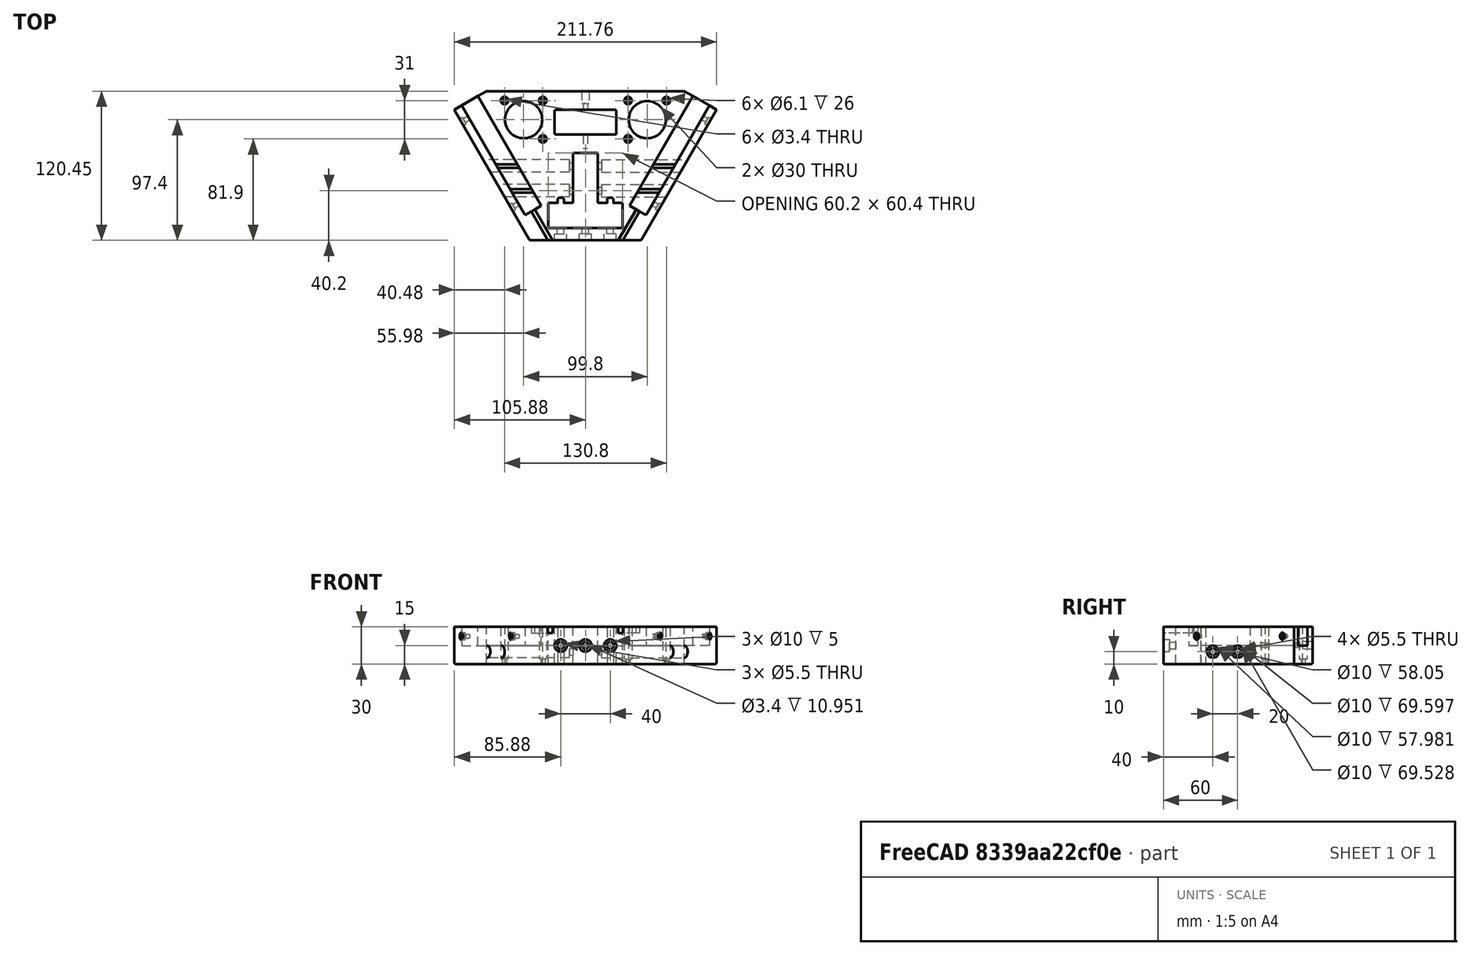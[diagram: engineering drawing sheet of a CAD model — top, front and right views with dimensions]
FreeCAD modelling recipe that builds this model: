
FCSTD DOCUMENT  (FreeCAD 2022.407R26244 +4693 (Git))
Label: as3top_corner
License: All rights reserved
LicenseURL: http://en.wikipedia.org/wiki/All_rights_reserved
objects: Part::FeaturePython×12, App::FeaturePython×2, Part::Feature×1
note: 12 computed .brp shape members not serialized (recipe doc carries the construction recipe); baked Part::Feature solids carry a one-line shape summary decoded from their .brp

FEATURE [App::FeaturePython] Constraints  # WARN: FeaturePython — macro-defined, semantics opaque (R4)
  TreeRank = 0
  _LinkVersion = 1
  _Version = 1
FEATURE [Part::Feature] ShapeCopy  label="TopCorner"
  Placement = pos=(-1.75e-14,-0.999998,-2.49e-14) rot=(0,0,1;0rad)
  TreeRank = 6
  shape: bbox 211.8 x 120.4 x 30 mm, 156 faces (baked)
FEATURE [Part::FeaturePython] Parts  # WARN: FeaturePython — macro-defined, semantics opaque (R4)
  Group = -> [ShapeCopy]
  GroupMode = 0
  TreeRank = 0
  _LinkVersion = 1
FEATURE [Part::FeaturePython] Assembly  label="As3TopCorner"  # WARN: FeaturePython — macro-defined, semantics opaque (R4)
  AutoRelax = true
  BuildShape = 0
  Freeze = false
  Group = -> [Constraints,Elements,Parts]
  TreeRank = 0
  Verbose = false
  _LinkVersion = 1
  _SolverType = 1
  _Version = 1
FEATURE [App::FeaturePython] Elements  # WARN: FeaturePython — macro-defined, semantics opaque (R4)
  Group = -> [Element,Element001,Element002,Element004,Element005,Element006,Element007,Element008,Element009,Element010]
  TreeRank = 0
  _LinkVersion = 1
FEATURE [Part::FeaturePython] Element  label="FaceHsup"  # link proxy (typed FeaturePython)
  Detach = false
  LinkTransform = true
  LinkedObject = -> ShapeCopy [Face23]
  TreeRank = 0
  _LinkVersion = 1
  _Parent = -> Elements
FEATURE [Part::FeaturePython] Element001  label="AppuiPoteau1"  # link proxy (typed FeaturePython)
  Detach = false
  LinkTransform = true
  LinkedObject = -> ShapeCopy [Face46]
  TreeRank = 0
  _LinkVersion = 1
  _Parent = -> Elements
FEATURE [Part::FeaturePython] Element002  label="AppuiPoteau2"  # link proxy (typed FeaturePython)
  Detach = false
  LinkTransform = true
  LinkedObject = -> ShapeCopy [Face44]
  TreeRank = 0
  _LinkVersion = 1
  _Parent = -> Elements
FEATURE [Part::FeaturePython] Element004  label="AppuiTravExtr1"  # link proxy (typed FeaturePython)
  Detach = false
  LinkTransform = true
  LinkedObject = -> ShapeCopy [Face18]
  TreeRank = 0
  _LinkVersion = 1
  _Parent = -> Elements
FEATURE [Part::FeaturePython] Element005  label="AppuiTrav1h"  # link proxy (typed FeaturePython)
  Detach = false
  LinkTransform = true
  LinkedObject = -> ShapeCopy [Face77]
  TreeRank = 0
  _LinkVersion = 1
  _Parent = -> Elements
FEATURE [Part::FeaturePython] Element006  label="AppuiTravExtr2"  # link proxy (typed FeaturePython)
  Detach = false
  LinkTransform = true
  LinkedObject = -> ShapeCopy [Face25]
  TreeRank = 0
  _LinkVersion = 1
  _Parent = -> Elements
FEATURE [Part::FeaturePython] Element007  label="AppuiTrav1v"  # link proxy (typed FeaturePython)
  Detach = false
  LinkTransform = true
  LinkedObject = -> ShapeCopy [Face27]
  TreeRank = 0
  _LinkVersion = 1
  _Parent = -> Elements
FEATURE [Part::FeaturePython] Element008  label="AppuiTrav2v"  # link proxy (typed FeaturePython)
  Detach = false
  LinkTransform = true
  LinkedObject = -> ShapeCopy [Face20]
  TreeRank = 0
  _LinkVersion = 1
  _Parent = -> Elements
FEATURE [Part::FeaturePython] Element009  label="AppuiLatPoteau21"  # link proxy (typed FeaturePython)
  Detach = false
  LinkTransform = true
  LinkedObject = -> ShapeCopy [Face33]
  TreeRank = 0
  _LinkVersion = 1
  _Parent = -> Elements
FEATURE [Part::FeaturePython] Element010  label="AppuiLatPoteau22"  # link proxy (typed FeaturePython)
  Detach = false
  LinkTransform = true
  LinkedObject = -> ShapeCopy [Face37]
  TreeRank = 0
  _LinkVersion = 1
  _Parent = -> Elements
